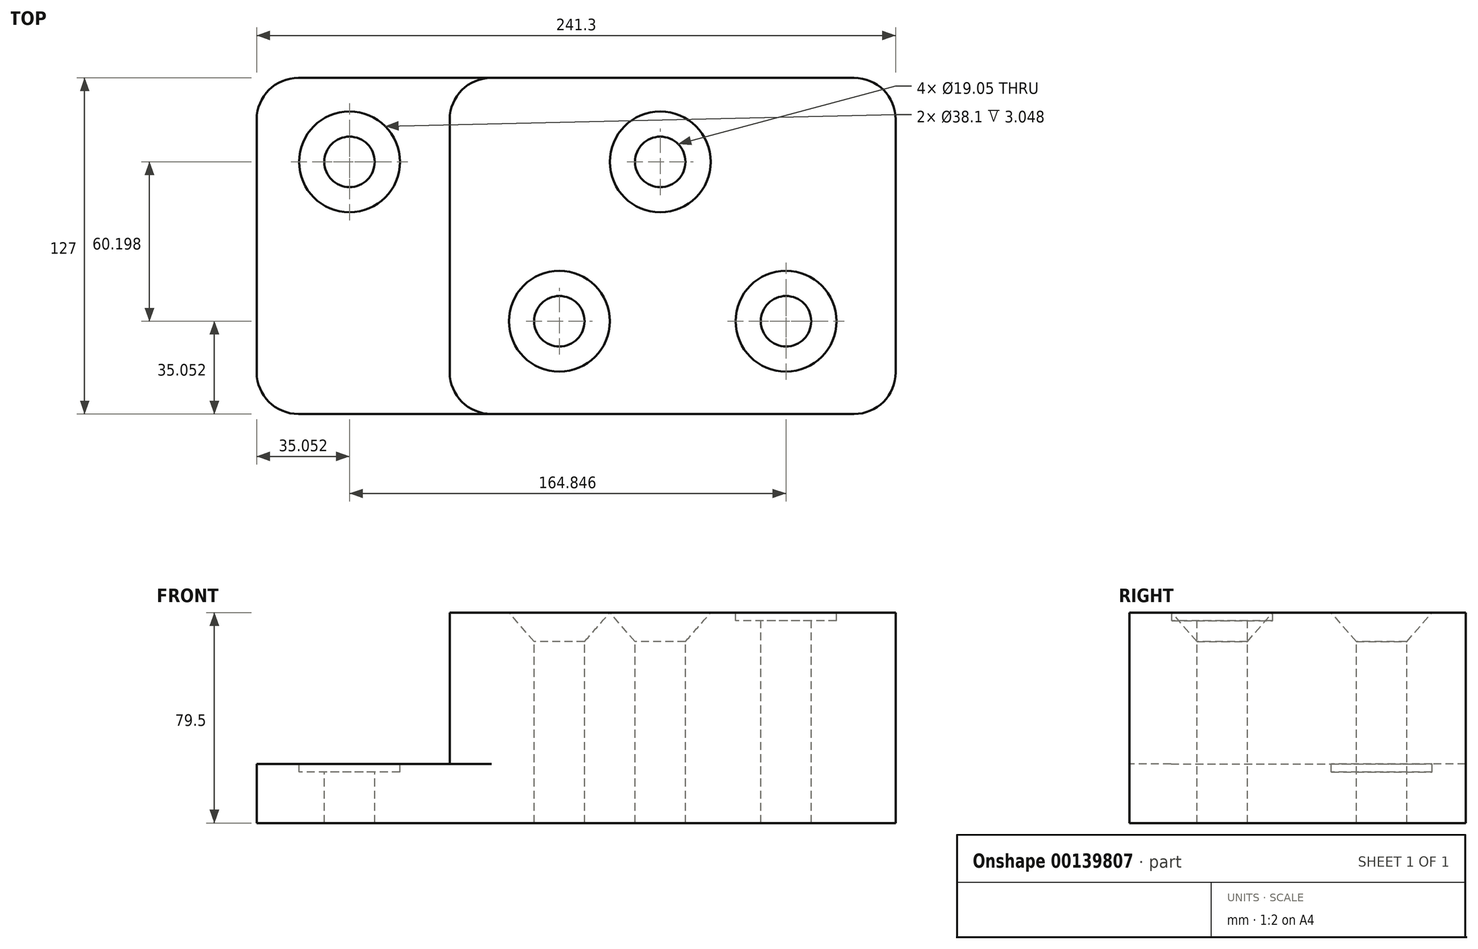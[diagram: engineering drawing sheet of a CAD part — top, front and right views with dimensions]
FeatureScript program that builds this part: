
annotation { "Feature Type Name" : "Feature", "Feature Type Description" : "" }
export const myFeature = defineFeature(function(context is Context, id is Id, definition is map)
    precondition{}
    {
        {
            var Q0;
            Q0=qCreatedBy(makeId("Top.planeOp"),FACE);
            var sketch = newSketch(context, id + "F0", { "sketchPlane" : qUnion([Q0])});
            skLineSegment(sketch, "E0.bottom", {"start": v(15.75, 0) * mm, "end": v(225.55, 0) * mm});
            skLineSegment(sketch, "E0.top", {"start": v(15.75, 127) * mm, "end": v(225.55, 127) * mm});
            skLineSegment(sketch, "E0.left", {"start": v(0, 15.75) * mm, "end": v(0, 111.25) * mm});
            skLineSegment(sketch, "E0.right", {"start": v(241.3, 15.75) * mm, "end": v(241.3, 111.25) * mm});
            skPoint(sketch, "E1.visualSharp", {"position": v(241.3, 127) * mm});
            skArc(sketch, "E1.filletArc", {"start": v(241.3, 111.25) * mm, "mid": v(236.69, 122.39) * mm, "end": v(225.55, 127) * mm});
            skPoint(sketch, "E2.visualSharp", {"position": v(241.3, 0) * mm});
            skArc(sketch, "E2.filletArc", {"start": v(225.55, 0) * mm, "mid": v(236.69, 4.61) * mm, "end": v(241.3, 15.75) * mm});
            skPoint(sketch, "E3.visualSharp", {"position": v(0, 0) * mm});
            skArc(sketch, "E3.filletArc", {"start": v(0, 15.75) * mm, "mid": v(4.61, 4.61) * mm, "end": v(15.75, 0) * mm});
            skPoint(sketch, "E4.visualSharp", {"position": v(0, 127) * mm});
            skArc(sketch, "E4.filletArc", {"start": v(15.75, 127) * mm, "mid": v(4.61, 122.39) * mm, "end": v(0, 111.25) * mm});
            skCircle(sketch, "E5", {"center": v(35.05, 95.25) * mm, "radius": 9.53 * mm, "construction": true});
            skSolve(sketch);
        }
        {
            var Q0;
            Q0=makeQuery(id+"F0.imprint","IMPRINT",FACE,{"disambiguationData":[TD([[makeQuery(id+"F0.imprint","IMPRINT",EDGE,{"derivedFrom":sQuery(id+"F0.wireOp",EDGE,"E0.bottom")}),1.0]])]});
            var Q1;
            Q1=makeQuery(id+"F0.imprint","IMPRINT",FACE,{"disambiguationData":[TD([[makeQuery(id+"F0.imprint","IMPRINT",EDGE,{"derivedFrom":sQuery(id+"F0.wireOp",EDGE,"E5")}),1.0]])]});
            extrude(context, id + "F1", {"entities" : qUnion([Q0, Q1]), "depth" : 22.35 * mm});
        }
        {
            var Q0;
            Q0=makeQuery(id+"F1.opExtrude","CAP_FACE",FACE,{"disambiguationData":[OSD([sQuery(id+"F0.wireOp",EDGE,"E0.bottom"),sQuery(id+"F0.wireOp",EDGE,"E0.top"),sQuery(id+"F0.wireOp",EDGE,"E0.left"),sQuery(id+"F0.wireOp",EDGE,"E0.right"),sQuery(id+"F0.wireOp",EDGE,"E1.filletArc"),sQuery(id+"F0.wireOp",EDGE,"E2.filletArc"),sQuery(id+"F0.wireOp",EDGE,"E3.filletArc"),sQuery(id+"F0.wireOp",EDGE,"E4.filletArc")])],"isStart":false});
            var sketch = newSketch(context, id + "F2", { "sketchPlane" : qUnion([Q0])});
            skLineSegment(sketch, "E6.bottom", {"start": v(88.65, 127) * mm, "end": v(225.55, 127) * mm});
            skLineSegment(sketch, "E6.top", {"start": v(88.65, 0) * mm, "end": v(225.55, 0) * mm});
            skLineSegment(sketch, "E6.left", {"start": v(72.9, 111.25) * mm, "end": v(72.9, 15.75) * mm});
            skLineSegment(sketch, "E6.right", {"start": v(241.3, 111.25) * mm, "end": v(241.3, 15.75) * mm});
            skPoint(sketch, "E7.visualSharp", {"position": v(241.3, 127) * mm});
            skArc(sketch, "E7.filletArc", {"start": v(241.3, 111.25) * mm, "mid": v(236.69, 122.39) * mm, "end": v(225.55, 127) * mm});
            skPoint(sketch, "E8.visualSharp", {"position": v(241.3, 0) * mm});
            skArc(sketch, "E8.filletArc", {"start": v(225.55, 0) * mm, "mid": v(236.69, 4.61) * mm, "end": v(241.3, 15.75) * mm});
            skPoint(sketch, "E9.visualSharp", {"position": v(72.9, 0) * mm});
            skArc(sketch, "E9.filletArc", {"start": v(72.9, 15.75) * mm, "mid": v(77.51, 4.61) * mm, "end": v(88.65, 0) * mm});
            skPoint(sketch, "E10.visualSharp", {"position": v(72.9, 127) * mm});
            skArc(sketch, "E10.filletArc", {"start": v(88.65, 127) * mm, "mid": v(77.51, 122.39) * mm, "end": v(72.9, 111.25) * mm});
            skCircle(sketch, "E11", {"center": v(199.9, 35.05) * mm, "radius": 9.53 * mm});
            skCircle(sketch, "E12", {"center": v(152.4, 95.25) * mm, "radius": 9.53 * mm});
            skCircle(sketch, "E13", {"center": v(114.3, 35.05) * mm, "radius": 9.53 * mm});
            skSolve(sketch);
        }
        {
            var Q0;
            Q0=makeQuery(id+"F2.imprint","IMPRINT",FACE,{"disambiguationData":[TD([[makeQuery(id+"F2.imprint","IMPRINT",EDGE,{"derivedFrom":sQuery(id+"F2.wireOp",EDGE,"E6.bottom")}),-1.0]])]});
            var Q1;
            Q1=makeQuery(id+"F2.imprint","IMPRINT",FACE,{"disambiguationData":[TD([[makeQuery(id+"F2.imprint","IMPRINT",EDGE,{"derivedFrom":sQuery(id+"F2.wireOp",EDGE,"E12")}),1.0]])]});
            var Q2;
            Q2=makeQuery(id+"F2.imprint","IMPRINT",FACE,{"disambiguationData":[TD([[makeQuery(id+"F2.imprint","IMPRINT",EDGE,{"derivedFrom":sQuery(id+"F2.wireOp",EDGE,"E13")}),1.0]])]});
            var Q3;
            Q3=makeQuery(id+"F2.imprint","IMPRINT",FACE,{"disambiguationData":[TD([[makeQuery(id+"F2.imprint","IMPRINT",EDGE,{"derivedFrom":sQuery(id+"F2.wireOp",EDGE,"E11")}),1.0]])]});
            extrude(context, id + "F3", {"entities" : qUnion([Q0, Q1, Q2, Q3]), "operationType" : NewBodyOperationType.ADD, "depth" : 57.15 * mm});
        }
        {
            var Q0;
            Q0=makeQuery(id+"F2.imprint","IMPRINT",FACE,{"disambiguationData":[TD([[makeQuery(id+"F2.imprint","IMPRINT",EDGE,{"derivedFrom":sQuery(id+"F2.wireOp",EDGE,"E6.left")}),-1.0]])]});
            var sketch = newSketch(context, id + "F4", { "sketchPlane" : qUnion([Q0])});
            skLineSegment(sketch, "E14.bottom", {"start": v(0, 0) * mm, "end": v(88.65, 0) * mm});
            skLineSegment(sketch, "E14.top", {"start": v(0, 127) * mm, "end": v(88.65, 127) * mm});
            skLineSegment(sketch, "E14.left", {"start": v(0, 0) * mm, "end": v(0, 127) * mm});
            skLineSegment(sketch, "E14.right", {"start": v(88.65, 0) * mm, "end": v(88.65, 127) * mm});
            skCircle(sketch, "E15", {"center": v(35.05, 95.25) * mm, "radius": 9.53 * mm});
            skSolve(sketch);
        }
        {
            var Q0;
            Q0=sQuery(id+"F4.wireOp",VERTEX,"E15.center");
            var Q1;
            Q1=makeQuery(id+"F1.opExtrude","SWEPT_BODY",BODY,{"disambiguationData":[OSD([sQuery(id+"F0.wireOp",EDGE,"E0.bottom"),sQuery(id+"F0.wireOp",EDGE,"E0.top"),sQuery(id+"F0.wireOp",EDGE,"E0.left"),sQuery(id+"F0.wireOp",EDGE,"E0.right"),sQuery(id+"F0.wireOp",EDGE,"E1.filletArc"),sQuery(id+"F0.wireOp",EDGE,"E2.filletArc"),sQuery(id+"F0.wireOp",EDGE,"E3.filletArc"),sQuery(id+"F0.wireOp",EDGE,"E4.filletArc")])]});
            hole(context, id + "F5", {"style" : HoleStyle.C_BORE, "endStyle" : HoleEndStyle.THROUGH, "holeDiameter" : 19.05 * mm, "cBoreDiameter" : 38.1 * mm, "cBoreDepth" : 3.05 * mm, "startFromSketch" : true, "locations" : qUnion([Q0]), "scope" : qUnion([Q1]), "isTappedThrough" : true});
        }
        {
            var Q0;
            Q0=makeQuery(id+"F3.opExtrude","CAP_FACE",FACE,{"disambiguationData":[OSD([sQuery(id+"F2.wireOp",EDGE,"E6.bottom"),sQuery(id+"F2.wireOp",EDGE,"E6.top"),sQuery(id+"F2.wireOp",EDGE,"E6.left"),sQuery(id+"F2.wireOp",EDGE,"E6.right"),sQuery(id+"F2.wireOp",EDGE,"E7.filletArc"),sQuery(id+"F2.wireOp",EDGE,"E8.filletArc"),sQuery(id+"F2.wireOp",EDGE,"E9.filletArc"),sQuery(id+"F2.wireOp",EDGE,"E10.filletArc")])],"isStart":false});
            var sketch = newSketch(context, id + "F6", { "sketchPlane" : qUnion([Q0])});
            skLineSegment(sketch, "E16.bottom", {"start": v(72.9, 0) * mm, "end": v(241.3, 0) * mm});
            skLineSegment(sketch, "E16.top", {"start": v(72.9, 127) * mm, "end": v(241.3, 127) * mm});
            skLineSegment(sketch, "E16.left", {"start": v(72.9, 0) * mm, "end": v(72.9, 127) * mm});
            skLineSegment(sketch, "E16.right", {"start": v(241.3, 0) * mm, "end": v(241.3, 127) * mm});
            skCircle(sketch, "E17", {"center": v(152.4, 95.25) * mm, "radius": 9.53 * mm});
            skCircle(sketch, "E18", {"center": v(114.3, 35.05) * mm, "radius": 9.53 * mm});
            skCircle(sketch, "E19", {"center": v(199.9, 35.05) * mm, "radius": 9.53 * mm});
            skSolve(sketch);
        }
        {
            var Q0;
            Q0=sQuery(id+"F6.wireOp",VERTEX,"E19.center");
            var Q1;
            Q1=makeQuery(id+"F1.opExtrude","SWEPT_BODY",BODY,{"disambiguationData":[OSD([sQuery(id+"F0.wireOp",EDGE,"E0.bottom"),sQuery(id+"F0.wireOp",EDGE,"E0.top"),sQuery(id+"F0.wireOp",EDGE,"E0.left"),sQuery(id+"F0.wireOp",EDGE,"E0.right"),sQuery(id+"F0.wireOp",EDGE,"E1.filletArc"),sQuery(id+"F0.wireOp",EDGE,"E2.filletArc"),sQuery(id+"F0.wireOp",EDGE,"E3.filletArc"),sQuery(id+"F0.wireOp",EDGE,"E4.filletArc")])]});
            hole(context, id + "F7", {"style" : HoleStyle.C_BORE, "endStyle" : HoleEndStyle.THROUGH, "holeDiameter" : 19.05 * mm, "cBoreDiameter" : 38.1 * mm, "cBoreDepth" : 3.05 * mm, "startFromSketch" : true, "locations" : qUnion([Q0]), "scope" : qUnion([Q1]), "isTappedThrough" : true});
        }
        {
            var Q0;
            Q0=sQuery(id+"F6.wireOp",VERTEX,"E17.center");
            var Q1;
            Q1=sQuery(id+"F6.wireOp",VERTEX,"E18.center");
            var Q2;
            Q2=makeQuery(id+"F1.opExtrude","SWEPT_BODY",BODY,{"disambiguationData":[OSD([sQuery(id+"F0.wireOp",EDGE,"E0.bottom"),sQuery(id+"F0.wireOp",EDGE,"E0.top"),sQuery(id+"F0.wireOp",EDGE,"E0.left"),sQuery(id+"F0.wireOp",EDGE,"E0.right"),sQuery(id+"F0.wireOp",EDGE,"E1.filletArc"),sQuery(id+"F0.wireOp",EDGE,"E2.filletArc"),sQuery(id+"F0.wireOp",EDGE,"E3.filletArc"),sQuery(id+"F0.wireOp",EDGE,"E4.filletArc")])]});
            hole(context, id + "F8", {"style" : HoleStyle.C_SINK, "endStyle" : HoleEndStyle.THROUGH, "holeDiameter" : 19.05 * mm, "cSinkDiameter" : 38.1 * mm, "cSinkAngle" : 82 * degree, "startFromSketch" : true, "locations" : qUnion([Q0, Q1]), "scope" : qUnion([Q2]), "isTappedThrough" : true});
        }
    });
